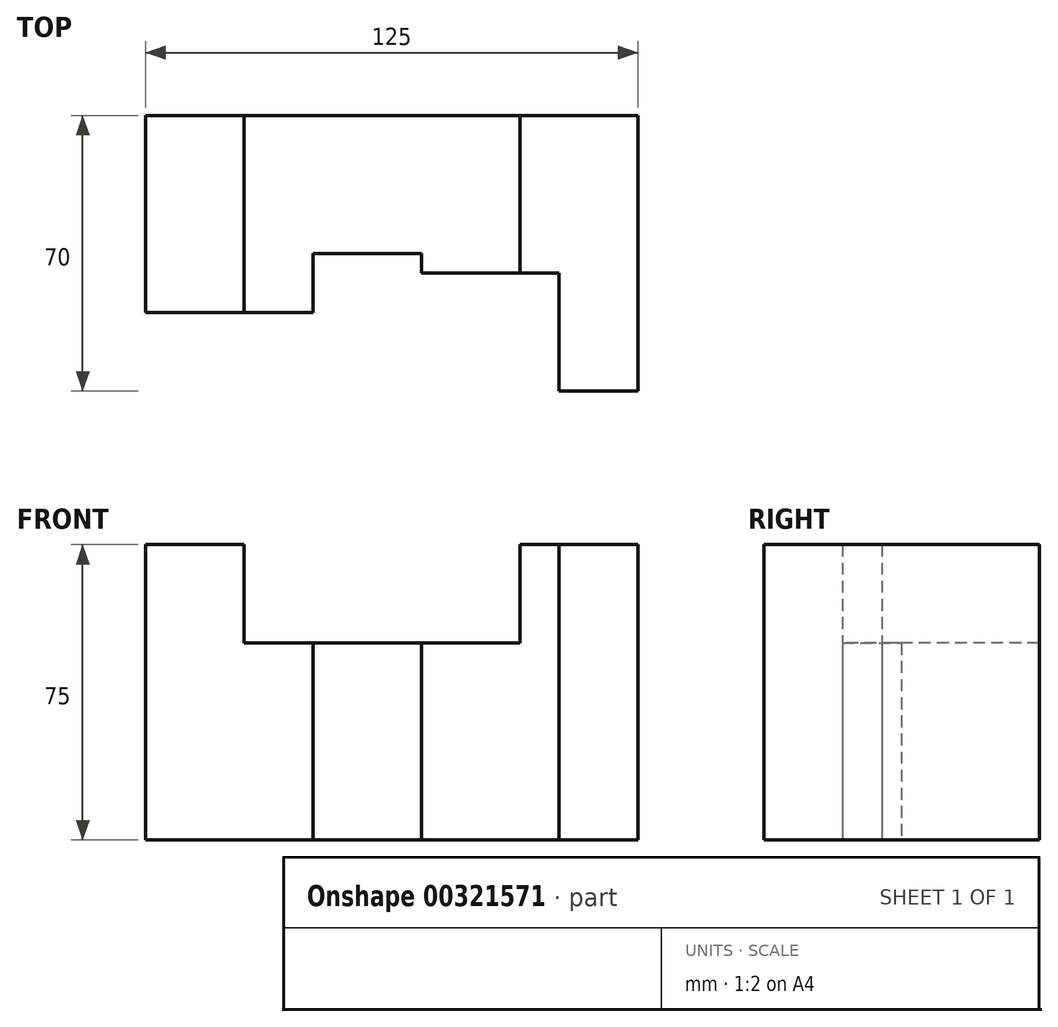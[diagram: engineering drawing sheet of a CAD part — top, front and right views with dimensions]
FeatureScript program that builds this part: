
annotation { "Feature Type Name" : "Feature", "Feature Type Description" : "" }
export const myFeature = defineFeature(function(context is Context, id is Id, definition is map)
    precondition{}
    {
        {
            var Q0;
            Q0=qCreatedBy(makeId("Top.planeOp"),FACE);
            var sketch = newSketch(context, id + "F0", { "sketchPlane" : qUnion([Q0])});
            skLineSegment(sketch, "E0", {"start": v(0, 0) * mm, "end": v(0, 50) * mm});
            skLineSegment(sketch, "E1", {"start": v(0, 50) * mm, "end": v(125, 50) * mm});
            skLineSegment(sketch, "E2", {"start": v(125, 50) * mm, "end": v(125, -20) * mm});
            skLineSegment(sketch, "E3", {"start": v(125, -20) * mm, "end": v(105, -20) * mm});
            skLineSegment(sketch, "E4", {"start": v(105, -20) * mm, "end": v(105, 10) * mm});
            skLineSegment(sketch, "E5", {"start": v(105, 10) * mm, "end": v(70, 10) * mm});
            skLineSegment(sketch, "E6", {"start": v(70, 10) * mm, "end": v(70, 15) * mm});
            skLineSegment(sketch, "E7", {"start": v(70, 15) * mm, "end": v(42.5, 15) * mm});
            skLineSegment(sketch, "E8", {"start": v(42.5, 15) * mm, "end": v(42.5, 0) * mm});
            skLineSegment(sketch, "E9", {"start": v(42.5, 0) * mm, "end": v(0, 0) * mm});
            skSolve(sketch);
        }
        {
            var Q0;
            Q0 = qSketchRegion(id + "F0", true);
            extrude(context, id + "F1", {"entities" : qUnion([Q0]), "depth" : 75 * mm});
        }
        {
            var Q0;
            Q0=makeQuery(id+"F1.opExtrude","SWEPT_FACE",FACE,{"disambiguationData":[OSD([sQuery(id+"F0.wireOp",EDGE,"E9")])]});
            var sketch = newSketch(context, id + "F2", { "sketchPlane" : qUnion([Q0])});
            skLineSegment(sketch, "E10.0.3", {"start": v(42.5, 50) * mm, "end": v(42.5, 40.01) * mm});
            skLineSegment(sketch, "E11", {"start": v(25, 75) * mm, "end": v(25, 50) * mm});
            skPoint(sketch, "E12.orphan", {"position": v(70, 0) * mm});
            skPoint(sketch, "E13.orphan", {"position": v(105, 0) * mm});
            skPoint(sketch, "E14.orphan", {"position": v(42.5, 0) * mm});
            skLineSegment(sketch, "E15", {"start": v(25, 50) * mm, "end": v(95, 50) * mm});
            skLineSegment(sketch, "E16", {"start": v(25, 75) * mm, "end": v(95, 75) * mm});
            skLineSegment(sketch, "E17", {"start": v(95, 75) * mm, "end": v(95, 50) * mm});
            skSolve(sketch);
        }
        {
            var Q0;
            Q0 = qSketchRegion(id + "F2", true);
            extrude(context, id + "F3", {"entities" : qUnion([Q0]), "operationType" : NewBodyOperationType.REMOVE, "endBound" : BoundingType.THROUGH_ALL, "oppositeDirection" : true, "depth" : 25 * mm});
        }
    });
